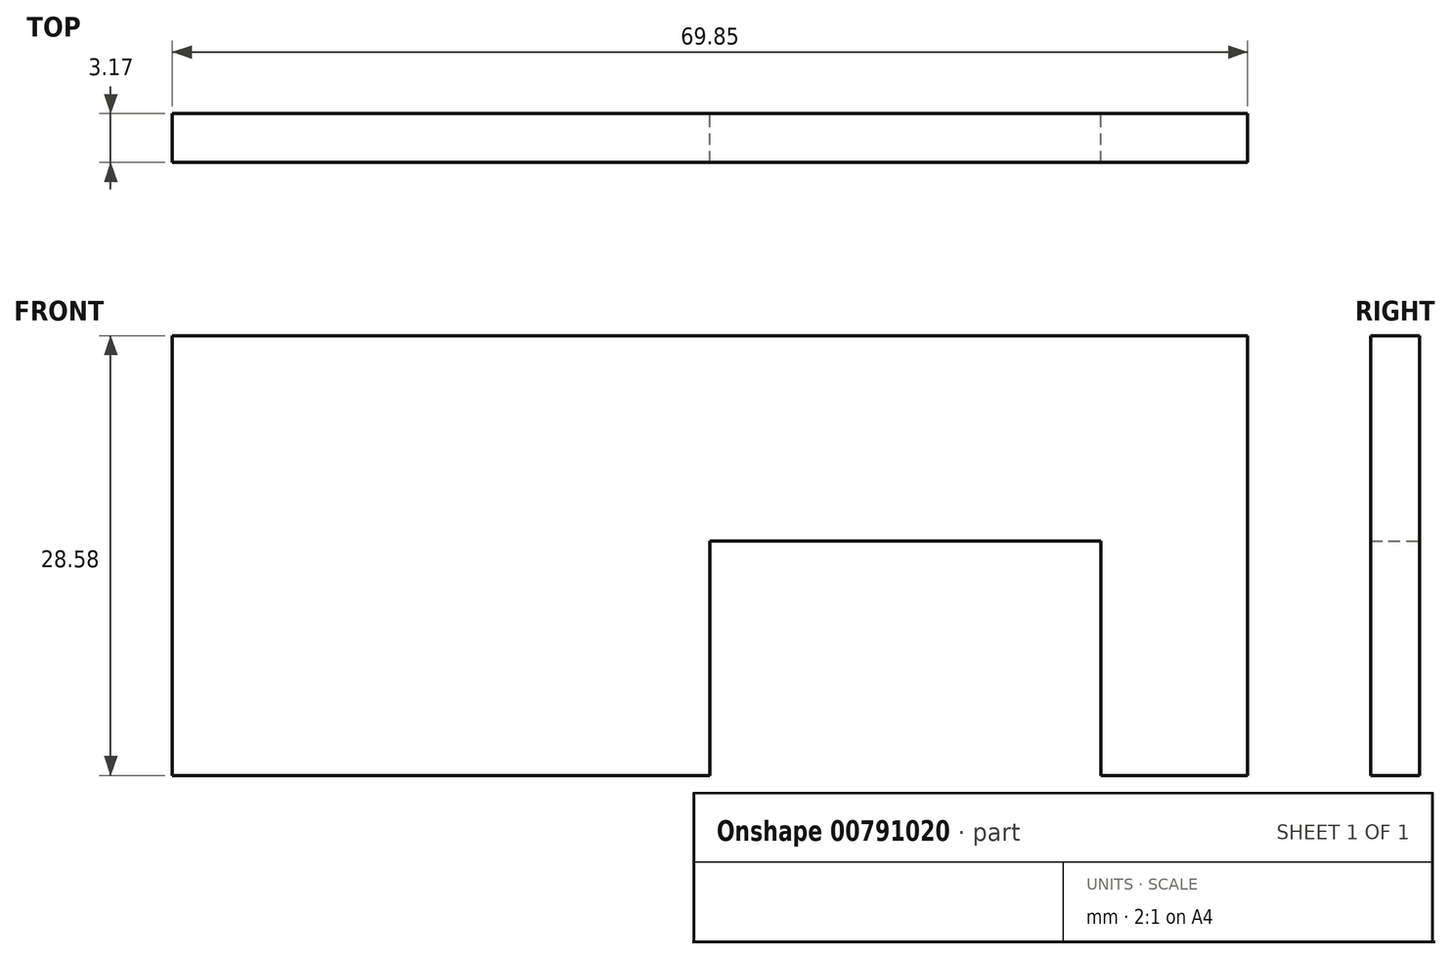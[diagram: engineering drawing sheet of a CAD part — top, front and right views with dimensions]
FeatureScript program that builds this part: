
annotation { "Feature Type Name" : "Feature", "Feature Type Description" : "" }
export const myFeature = defineFeature(function(context is Context, id is Id, definition is map)
    precondition{}
    {
        {
            var Q0;
            Q0=qCreatedBy(makeId("Front.planeOp"),FACE);
            var sketch = newSketch(context, id + "F0", { "sketchPlane" : qUnion([Q0])});
            skLineSegment(sketch, "E0.bottom", {"start": v(12.7, -7.62) * mm, "end": v(-12.7, -7.62) * mm});
            skLineSegment(sketch, "E0.top", {"start": v(12.7, 7.62) * mm, "end": v(-12.7, 7.62) * mm});
            skLineSegment(sketch, "E0.left", {"start": v(12.7, -7.62) * mm, "end": v(12.7, 7.62) * mm});
            skLineSegment(sketch, "E0.right", {"start": v(-12.7, -7.62) * mm, "end": v(-12.7, 7.62) * mm});
            skPoint(sketch, "E0.middle", {"position": v(0, 0) * mm});
            skLineSegment(sketch, "E1.bottom", {"start": v(22.23, -7.62) * mm, "end": v(-47.62, -7.62) * mm});
            skLineSegment(sketch, "E1.top", {"start": v(22.23, 20.96) * mm, "end": v(-47.62, 20.96) * mm});
            skLineSegment(sketch, "E1.left", {"start": v(22.23, -7.62) * mm, "end": v(22.22, 20.96) * mm});
            skLineSegment(sketch, "E1.right", {"start": v(-47.62, -7.62) * mm, "end": v(-47.62, 20.96) * mm});
            skLineSegment(sketch, "E2", {"start": v(12.7, 0) * mm, "end": v(0, 0) * mm});
            skLineSegment(sketch, "E3", {"start": v(12.7, 0) * mm, "end": v(3.18, 0) * mm});
            skLineSegment(sketch, "E4", {"start": v(3.18, 0) * mm, "end": v(19.05, 0) * mm});
            skSolve(sketch);
        }
        {
            var Q0;
            {var subQ0=sQuery(id+"F0.wireOp",EDGE,"E1.bottom");var subQ1=sQuery(id+"F0.wireOp",EDGE,"E0.right");var subQ2=makeQuery(id+"F0.imprint","INTERSECT",VERTEX,{"derivedFrom":[subQ1,subQ0]});Q0=makeQuery(id+"F0.imprint","IMPRINT",FACE,{"disambiguationData":[TD([[makeQuery(id+"F0.imprint","IMPRINT",EDGE,{"disambiguationData":[TD([[subQ2,-1.0]])],"derivedFrom":subQ0}),-1.0]])]});}
            var Q1;
            Q1=makeQuery(id+"F0.imprint","IMPRINT",FACE,{"disambiguationData":[TD([[makeQuery(id+"F0.imprint","IMPRINT",EDGE,{"derivedFrom":sQuery(id+"F0.wireOp",EDGE,"E1.top")}),1.0]])]});
            var Q2;
            {var subQ0=sQuery(id+"F0.wireOp",EDGE,"pS572jdx-SKgW-zBj2-Zjhw-WW2dHY2xkwCR");var subQ1=sQuery(id+"F0.wireOp",EDGE,"E0.top");var subQ2=makeQuery(id+"F0.imprint","INTERSECT",VERTEX,{"disambiguationData":[OD(0.0)],"derivedFrom":[subQ1,subQ0]});Q2=makeQuery(id+"F0.imprint","IMPRINT",FACE,{"disambiguationData":[TD([[makeQuery(id+"F0.imprint","IMPRINT",EDGE,{"disambiguationData":[TD([[subQ2,-1.0]])],"derivedFrom":subQ1}),-1.0]])]});}
            var Q3;
            {var subQ0=sQuery(id+"F0.wireOp",EDGE,"pS572jdx-SKgW-zBj2-Zjhw-WW2dHY2xkwCR");var subQ1=sQuery(id+"F0.wireOp",EDGE,"E1.bottom");var subQ2=makeQuery(id+"F0.imprint","INTERSECT",VERTEX,{"disambiguationData":[OD(1.0)],"derivedFrom":[subQ1,subQ0]});Q3=makeQuery(id+"F0.imprint","IMPRINT",FACE,{"disambiguationData":[TD([[makeQuery(id+"F0.imprint","IMPRINT",EDGE,{"disambiguationData":[TD([[subQ2,-1.0]])],"derivedFrom":subQ1}),-1.0]])]});}
            var Q4;
            {var subQ0=sQuery(id+"F0.wireOp",EDGE,"ldDDFbeM-xfDS-kZqO-mGzn-hNgQm2YPC7GP");var subQ1=sQuery(id+"F0.wireOp",EDGE,"E1.bottom");var subQ2=makeQuery(id+"F0.imprint","INTERSECT",VERTEX,{"disambiguationData":[OD(0.0)],"derivedFrom":[subQ1,subQ0]});Q4=makeQuery(id+"F0.imprint","IMPRINT",FACE,{"disambiguationData":[TD([[makeQuery(id+"F0.imprint","IMPRINT",EDGE,{"disambiguationData":[TD([[subQ2,-1.0]])],"derivedFrom":subQ1}),-1.0]])]});}
            extrude(context, id + "F1", {"entities" : qUnion([Q0, Q1, Q2, Q3, Q4]), "depth" : 3.17 * mm, "offsetDistance" : 25.4 * mm});
        }
    });
